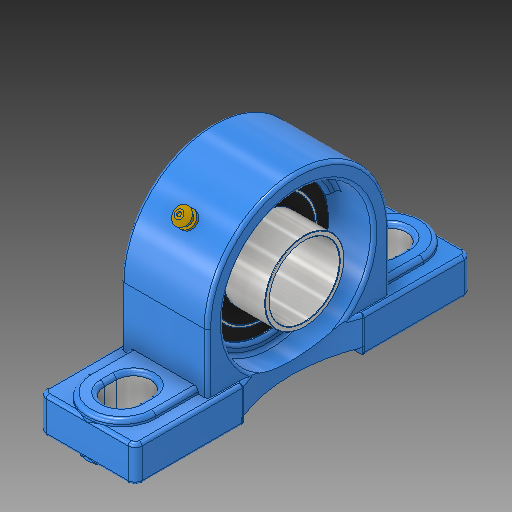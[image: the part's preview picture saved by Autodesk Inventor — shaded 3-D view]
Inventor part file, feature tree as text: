
AUTODESK INVENTOR PART (.ipt)
format: ipt  version: 2019 (Build 230136000, 136)  size: 666,624 bytes
history: native  units: in
note: dims shown in document units (in); Inventor stores cm internally (conversion verified against a paired STEP export)
features: sketch x28, plane x7, other x3
ambient origin geometry x8: Origin, YZ Plane, XZ Plane, XY Plane, X Axis, Y Axis, Z Axis, Center Point
bodies: Solid1 (feature_tree)
feature tree (38):
  other  "Pillow Bearing inventor.ipt"
  other  "Solid1::Pillow Bearing inventor.ipt"
  other  "TaggingFeature1"
  sketch  "Sketch1"  dims[d0=0.3937in]
  sketch  "Sketch2"
  sketch  "Sketch3"
  sketch  "Sketch4"
  sketch  "Sketch5"
  sketch  "Sketch6"
  sketch  "Sketch7"
  sketch  "Sketch8"
  sketch  "Sketch9"
  sketch  "Sketch10"
  sketch  "Sketch11"
  sketch  "Sketch13"
  sketch  "Sketch14"
  sketch  "Sketch15"
  sketch  "Sketch17"
  sketch  "Sketch18"
  sketch  "Sketch19"
  sketch  "Sketch20"
  sketch  "Sketch21"
  sketch  "Sketch22"
  sketch  "Sketch23"
  sketch  "Sketch24"
  sketch  "Sketch25"
  sketch  "Sketch26"
  sketch  "Sketch27"
  sketch  "Sketch28"
  sketch  "Sketch29"
  sketch  "Sketch30"
  plane  "Work Plane1"
  plane  "Work Plane2"
  plane  "Work Plane5"
  plane  "Work Plane6"
  plane  "Work Plane7"
  plane  "Work Plane8"
  plane  "Work Plane9"
